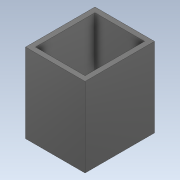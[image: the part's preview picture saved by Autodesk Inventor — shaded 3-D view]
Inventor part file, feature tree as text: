
AUTODESK INVENTOR PART (.ipt)
format: ipt  version: 2020 (Build 240168000, 168)  size: 119,808 bytes
history: native  units: mm
features: extrude x3, sketch x3
ambient origin geometry x8: Origin, YZ Plane, XZ Plane, XY Plane, X Axis, Y Axis, Z Axis, Center Point
bodies: Volumenkörper1 (feature_tree)
feature tree (6):
  extrude  "Extrusion1"  Depth=160.0mm
  extrude  "Extrusion2"  Depth=10.0mm
  extrude  "Extrusion3"  Depth=10.0mm
  sketch  "Skizze1"  dims[d0=120.0mm d1=160.0mm]
  sketch  "Skizze2"  dims[d2=140.0mm d3=0.0mm d4=10.0mm]
  sketch  "Skizze3"  dims[d5=10.0mm d6=10.0mm d7=30.0mm d8=130.0mm d9=0.0mm d10=10.0mm d11=10.0mm d12=10.0mm d13=10.0mm d14=130.0mm d15=0.0mm]
